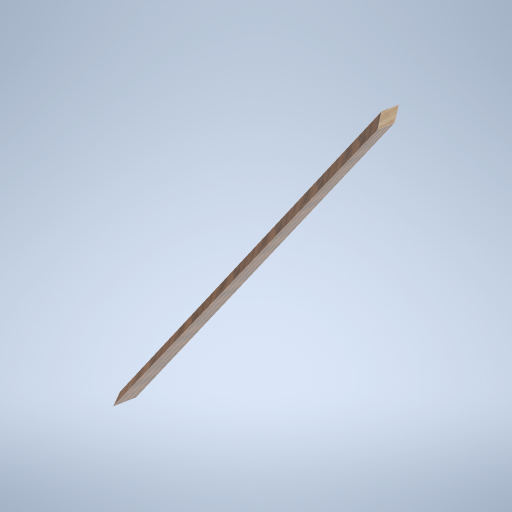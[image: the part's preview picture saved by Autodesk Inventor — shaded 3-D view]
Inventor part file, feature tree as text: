
AUTODESK INVENTOR PART (.ipt)
format: ipt  version: 2024.2 (Build 282272000, 272)  size: 289,792 bytes
history: native  units: mm
features: sketch x4, plane x2, loft x1
ambient origin geometry x8: Origin, YZ Plane, XZ Plane, XY Plane, X Axis, Y Axis, Z Axis, Center Point
bodies: Solid1 (feature_tree)
feature tree (7):
  sketch  "Sketch1"  dims[d0=0.0mm d1=1791.0mm d2=0.0mm d3=90.0deg]
  plane  "Work Plane2"
  loft  "Loft1"
  sketch  "Sketch4"
  plane  "Work Plane1"
  sketch  "Sketch2"  dims[d4=0.0mm d5=90.0deg]
  sketch  "Sketch3"
